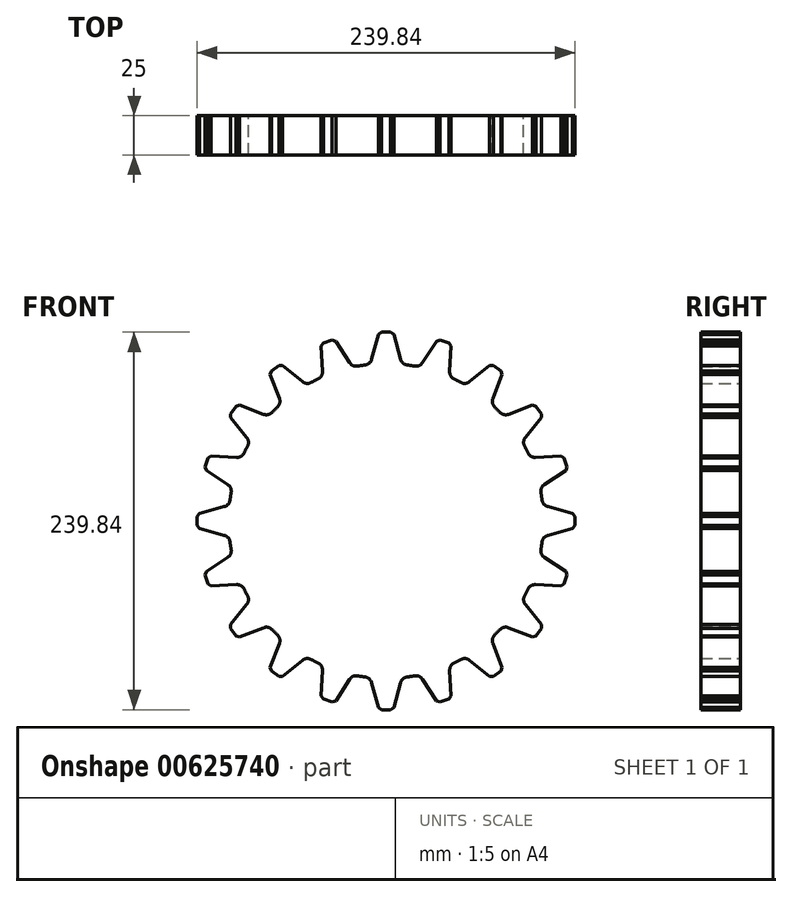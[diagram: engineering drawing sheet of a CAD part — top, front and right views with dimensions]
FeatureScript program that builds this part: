
annotation { "Feature Type Name" : "Feature", "Feature Type Description" : "" }
export const myFeature = defineFeature(function(context is Context, id is Id, definition is map)
    precondition{}
    {
        {
            var Q0;
            Q0=qCreatedBy(makeId("Front.planeOp"),FACE);
            var sketch = newSketch(context, id + "F0", { "sketchPlane" : qUnion([Q0])});
            skCircle(sketch, "E0", {"center": v(0, 0) * mm, "radius": 100 * mm});
            skCircle(sketch, "E1", {"center": v(0, 0) * mm, "radius": 120 * mm, "construction": true});
            skLineSegment(sketch, "E2", {"start": v(0, 0) * mm, "end": v(0, 167.9) * mm, "construction": true});
            skLineSegment(sketch, "E3", {"start": v(-4.5, 119.92) * mm, "end": v(-9.97, 99.5) * mm});
            skLineSegment(sketch, "E4.MirrorCS", {"start": v(4.5, 119.92) * mm, "end": v(9.97, 99.5) * mm});
            skLineSegment(sketch, "E5", {"start": v(-4.5, 119.92) * mm, "end": v(4.5, 119.92) * mm});
            skLineSegment(sketch, "E6.1.0", {"start": v(-41.34, 112.66) * mm, "end": v(-40.23, 91.55) * mm});
            skLineSegment(sketch, "E6.1.1", {"start": v(-32.78, 115.44) * mm, "end": v(-21.27, 97.71) * mm});
            skLineSegment(sketch, "E6.2.0", {"start": v(-74.13, 94.37) * mm, "end": v(-66.55, 74.64) * mm});
            skLineSegment(sketch, "E6.2.1", {"start": v(-66.84, 99.66) * mm, "end": v(-50.42, 86.36) * mm});
            skLineSegment(sketch, "E7.2.3.0", {"start": v(-99.66, 66.84) * mm, "end": v(-86.36, 50.42) * mm});
            skLineSegment(sketch, "E7.3.3.0", {"start": v(-94.37, 74.13) * mm, "end": v(-74.64, 66.55) * mm});
            skLineSegment(sketch, "E7.2.4.0", {"start": v(-115.44, 32.78) * mm, "end": v(-97.71, 21.27) * mm});
            skLineSegment(sketch, "E7.3.4.0", {"start": v(-112.66, 41.34) * mm, "end": v(-91.55, 40.23) * mm});
            skLineSegment(sketch, "E7.2.5.0", {"start": v(-119.92, -4.5) * mm, "end": v(-99.5, -9.97) * mm});
            skLineSegment(sketch, "E7.3.5.0", {"start": v(-119.92, 4.5) * mm, "end": v(-99.5, 9.97) * mm});
            skLineSegment(sketch, "E7.2.6.0", {"start": v(-112.66, -41.34) * mm, "end": v(-91.55, -40.23) * mm});
            skLineSegment(sketch, "E7.3.6.0", {"start": v(-115.44, -32.78) * mm, "end": v(-97.71, -21.27) * mm});
            skLineSegment(sketch, "E7.2.7.0", {"start": v(-94.37, -74.13) * mm, "end": v(-74.64, -66.55) * mm});
            skLineSegment(sketch, "E7.3.7.0", {"start": v(-99.66, -66.84) * mm, "end": v(-86.36, -50.42) * mm});
            skLineSegment(sketch, "E7.2.8.0", {"start": v(-66.84, -99.66) * mm, "end": v(-50.42, -86.36) * mm});
            skLineSegment(sketch, "E7.3.8.0", {"start": v(-74.13, -94.37) * mm, "end": v(-66.55, -74.64) * mm});
            skLineSegment(sketch, "E7.2.9.0", {"start": v(-32.78, -115.44) * mm, "end": v(-21.27, -97.71) * mm});
            skLineSegment(sketch, "E7.3.9.0", {"start": v(-41.34, -112.66) * mm, "end": v(-40.23, -91.55) * mm});
            skLineSegment(sketch, "E7.2.10.0", {"start": v(4.5, -119.92) * mm, "end": v(9.97, -99.5) * mm});
            skLineSegment(sketch, "E7.3.10.0", {"start": v(-4.5, -119.92) * mm, "end": v(-9.97, -99.5) * mm});
            skLineSegment(sketch, "E7.2.11.0", {"start": v(41.34, -112.66) * mm, "end": v(40.23, -91.55) * mm});
            skLineSegment(sketch, "E7.3.11.0", {"start": v(32.78, -115.44) * mm, "end": v(21.27, -97.71) * mm});
            skLineSegment(sketch, "E7.2.12.0", {"start": v(74.13, -94.37) * mm, "end": v(66.55, -74.64) * mm});
            skLineSegment(sketch, "E7.3.12.0", {"start": v(66.84, -99.66) * mm, "end": v(50.42, -86.36) * mm});
            skLineSegment(sketch, "E7.2.13.0", {"start": v(99.66, -66.84) * mm, "end": v(86.36, -50.42) * mm});
            skLineSegment(sketch, "E7.3.13.0", {"start": v(94.37, -74.13) * mm, "end": v(74.64, -66.55) * mm});
            skLineSegment(sketch, "E7.2.14.0", {"start": v(115.44, -32.78) * mm, "end": v(97.71, -21.27) * mm});
            skLineSegment(sketch, "E7.3.14.0", {"start": v(112.66, -41.34) * mm, "end": v(91.55, -40.23) * mm});
            skLineSegment(sketch, "E7.2.15.0", {"start": v(119.92, 4.5) * mm, "end": v(99.5, 9.97) * mm});
            skLineSegment(sketch, "E7.3.15.0", {"start": v(119.92, -4.5) * mm, "end": v(99.5, -9.97) * mm});
            skLineSegment(sketch, "E7.2.16.0", {"start": v(112.66, 41.34) * mm, "end": v(91.55, 40.23) * mm});
            skLineSegment(sketch, "E7.3.16.0", {"start": v(115.44, 32.78) * mm, "end": v(97.71, 21.27) * mm});
            skLineSegment(sketch, "E7.2.17.0", {"start": v(94.37, 74.13) * mm, "end": v(74.64, 66.55) * mm});
            skLineSegment(sketch, "E7.3.17.0", {"start": v(99.66, 66.84) * mm, "end": v(86.36, 50.42) * mm});
            skLineSegment(sketch, "E7.2.18.0", {"start": v(66.84, 99.66) * mm, "end": v(50.42, 86.36) * mm});
            skLineSegment(sketch, "E7.3.18.0", {"start": v(74.13, 94.37) * mm, "end": v(66.55, 74.64) * mm});
            skLineSegment(sketch, "E7.2.19.0", {"start": v(32.78, 115.44) * mm, "end": v(21.27, 97.71) * mm});
            skLineSegment(sketch, "E7.3.19.0", {"start": v(41.34, 112.66) * mm, "end": v(40.23, 91.55) * mm});
            skLineSegment(sketch, "E8", {"start": v(32.78, 115.44) * mm, "end": v(41.34, 112.66) * mm});
            skLineSegment(sketch, "E9", {"start": v(66.84, 99.66) * mm, "end": v(74.13, 94.37) * mm});
            skLineSegment(sketch, "E10", {"start": v(94.37, 74.13) * mm, "end": v(99.66, 66.84) * mm});
            skLineSegment(sketch, "E11", {"start": v(112.66, 41.34) * mm, "end": v(115.44, 32.78) * mm});
            skLineSegment(sketch, "E12", {"start": v(119.92, 4.5) * mm, "end": v(119.92, -4.5) * mm});
            skLineSegment(sketch, "E13", {"start": v(115.44, -32.78) * mm, "end": v(112.66, -41.34) * mm});
            skLineSegment(sketch, "E14", {"start": v(94.37, -74.13) * mm, "end": v(99.66, -66.84) * mm});
            skLineSegment(sketch, "E15", {"start": v(74.13, -94.37) * mm, "end": v(66.84, -99.66) * mm});
            skLineSegment(sketch, "E16", {"start": v(41.34, -112.66) * mm, "end": v(32.78, -115.44) * mm});
            skLineSegment(sketch, "E17", {"start": v(4.5, -119.92) * mm, "end": v(-4.5, -119.92) * mm});
            skLineSegment(sketch, "E18", {"start": v(-32.78, -115.44) * mm, "end": v(-41.34, -112.66) * mm});
            skLineSegment(sketch, "E19", {"start": v(-66.84, -99.66) * mm, "end": v(-74.13, -94.37) * mm});
            skLineSegment(sketch, "E20", {"start": v(-94.37, -74.13) * mm, "end": v(-99.66, -66.84) * mm});
            skLineSegment(sketch, "E21", {"start": v(-112.66, -41.34) * mm, "end": v(-115.44, -32.78) * mm});
            skLineSegment(sketch, "E22", {"start": v(-119.92, -4.5) * mm, "end": v(-119.92, 4.5) * mm});
            skLineSegment(sketch, "E23", {"start": v(-115.44, 32.78) * mm, "end": v(-112.66, 41.34) * mm});
            skLineSegment(sketch, "E24", {"start": v(-99.66, 66.84) * mm, "end": v(-94.37, 74.13) * mm});
            skLineSegment(sketch, "E25", {"start": v(-74.13, 94.37) * mm, "end": v(-66.84, 99.66) * mm});
            skLineSegment(sketch, "E26", {"start": v(-41.34, 112.66) * mm, "end": v(-32.78, 115.44) * mm});
            skSolve(sketch);
        }
        {
            var Q0;
            Q0 = qSketchRegion(id + "F0", true);
            extrude(context, id + "F1", {"entities" : qUnion([Q0]), "depth" : 25 * mm, "offsetDistance" : 25 * mm});
        }
        {
            var Q0;
            Q0=makeQuery(id+"F1.opExtrude","SWEPT_EDGE",EDGE,{"disambiguationData":[OSD([sQuery(id+"F0.wireOp",EDGE,"E7.2.18.0"),sQuery(id+"F0.wireOp",EDGE,"E9")])]});
            var Q1;
            Q1=makeQuery(id+"F1.opExtrude","SWEPT_EDGE",EDGE,{"disambiguationData":[OSD([sQuery(id+"F0.wireOp",EDGE,"E7.3.18.0"),sQuery(id+"F0.wireOp",EDGE,"E9")])]});
            chamfer(context, id + "F2", {"entities" : qUnion([Q0, Q1]), "width" : 2 * mm, "tangentPropagation" : true});
        }
        {
            var Q0;
            Q0=makeQuery(id+"F1.opExtrude","SWEPT_EDGE",EDGE,{"disambiguationData":[OSD([sQuery(id+"F0.wireOp",EDGE,"E7.2.17.0"),sQuery(id+"F0.wireOp",EDGE,"E10")])]});
            var Q1;
            Q1=makeQuery(id+"F1.opExtrude","SWEPT_EDGE",EDGE,{"disambiguationData":[OSD([sQuery(id+"F0.wireOp",EDGE,"E7.3.17.0"),sQuery(id+"F0.wireOp",EDGE,"E10")])]});
            var Q2;
            Q2=makeQuery(id+"F1.opExtrude","SWEPT_EDGE",EDGE,{"disambiguationData":[OSD([sQuery(id+"F0.wireOp",EDGE,"E7.2.16.0"),sQuery(id+"F0.wireOp",EDGE,"E11")])]});
            var Q3;
            Q3=makeQuery(id+"F1.opExtrude","SWEPT_EDGE",EDGE,{"disambiguationData":[OSD([sQuery(id+"F0.wireOp",EDGE,"E7.3.16.0"),sQuery(id+"F0.wireOp",EDGE,"E11")])]});
            var Q4;
            Q4=makeQuery(id+"F1.opExtrude","SWEPT_EDGE",EDGE,{"disambiguationData":[OSD([sQuery(id+"F0.wireOp",EDGE,"E7.2.15.0"),sQuery(id+"F0.wireOp",EDGE,"E12")])]});
            var Q5;
            Q5=makeQuery(id+"F1.opExtrude","SWEPT_EDGE",EDGE,{"disambiguationData":[OSD([sQuery(id+"F0.wireOp",EDGE,"E7.3.15.0"),sQuery(id+"F0.wireOp",EDGE,"E12")])]});
            var Q6;
            Q6=makeQuery(id+"F1.opExtrude","SWEPT_EDGE",EDGE,{"disambiguationData":[OSD([sQuery(id+"F0.wireOp",EDGE,"E7.2.14.0"),sQuery(id+"F0.wireOp",EDGE,"E13")])]});
            var Q7;
            Q7=makeQuery(id+"F1.opExtrude","SWEPT_EDGE",EDGE,{"disambiguationData":[OSD([sQuery(id+"F0.wireOp",EDGE,"E7.3.14.0"),sQuery(id+"F0.wireOp",EDGE,"E13")])]});
            var Q8;
            Q8=makeQuery(id+"F1.opExtrude","SWEPT_EDGE",EDGE,{"disambiguationData":[OSD([sQuery(id+"F0.wireOp",EDGE,"E7.2.13.0"),sQuery(id+"F0.wireOp",EDGE,"E14")])]});
            var Q9;
            Q9=makeQuery(id+"F1.opExtrude","SWEPT_EDGE",EDGE,{"disambiguationData":[OSD([sQuery(id+"F0.wireOp",EDGE,"E7.3.13.0"),sQuery(id+"F0.wireOp",EDGE,"E14")])]});
            var Q10;
            Q10=makeQuery(id+"F1.opExtrude","SWEPT_EDGE",EDGE,{"disambiguationData":[OSD([sQuery(id+"F0.wireOp",EDGE,"E7.2.12.0"),sQuery(id+"F0.wireOp",EDGE,"E15")])]});
            var Q11;
            Q11=makeQuery(id+"F1.opExtrude","SWEPT_EDGE",EDGE,{"disambiguationData":[OSD([sQuery(id+"F0.wireOp",EDGE,"E7.3.12.0"),sQuery(id+"F0.wireOp",EDGE,"E15")])]});
            var Q12;
            Q12=makeQuery(id+"F1.opExtrude","SWEPT_EDGE",EDGE,{"disambiguationData":[OSD([sQuery(id+"F0.wireOp",EDGE,"E7.2.11.0"),sQuery(id+"F0.wireOp",EDGE,"E16")])]});
            var Q13;
            Q13=makeQuery(id+"F1.opExtrude","SWEPT_EDGE",EDGE,{"disambiguationData":[OSD([sQuery(id+"F0.wireOp",EDGE,"E7.3.11.0"),sQuery(id+"F0.wireOp",EDGE,"E16")])]});
            chamfer(context, id + "F3", {"entities" : qUnion([Q0, Q1, Q2, Q3, Q4, Q5, Q6, Q7, Q8, Q9, Q10, Q11, Q12, Q13]), "width" : 2 * mm, "tangentPropagation" : true});
        }
        {
            var Q0;
            Q0=makeQuery(id+"F1.opExtrude","SWEPT_EDGE",EDGE,{"disambiguationData":[OSD([sQuery(id+"F0.wireOp",EDGE,"E7.2.10.0"),sQuery(id+"F0.wireOp",EDGE,"E17")])]});
            var Q1;
            Q1=makeQuery(id+"F1.opExtrude","SWEPT_EDGE",EDGE,{"disambiguationData":[OSD([sQuery(id+"F0.wireOp",EDGE,"E7.3.10.0"),sQuery(id+"F0.wireOp",EDGE,"E17")])]});
            var Q2;
            Q2=makeQuery(id+"F1.opExtrude","SWEPT_EDGE",EDGE,{"disambiguationData":[OSD([sQuery(id+"F0.wireOp",EDGE,"E7.2.9.0"),sQuery(id+"F0.wireOp",EDGE,"E18")])]});
            var Q3;
            Q3=makeQuery(id+"F1.opExtrude","SWEPT_EDGE",EDGE,{"disambiguationData":[OSD([sQuery(id+"F0.wireOp",EDGE,"E7.3.9.0"),sQuery(id+"F0.wireOp",EDGE,"E18")])]});
            var Q4;
            Q4=makeQuery(id+"F1.opExtrude","SWEPT_EDGE",EDGE,{"disambiguationData":[OSD([sQuery(id+"F0.wireOp",EDGE,"E7.2.8.0"),sQuery(id+"F0.wireOp",EDGE,"E19")])]});
            var Q5;
            Q5=makeQuery(id+"F1.opExtrude","SWEPT_EDGE",EDGE,{"disambiguationData":[OSD([sQuery(id+"F0.wireOp",EDGE,"E7.3.8.0"),sQuery(id+"F0.wireOp",EDGE,"E19")])]});
            var Q6;
            Q6=makeQuery(id+"F1.opExtrude","SWEPT_EDGE",EDGE,{"disambiguationData":[OSD([sQuery(id+"F0.wireOp",EDGE,"E7.2.7.0"),sQuery(id+"F0.wireOp",EDGE,"E20")])]});
            var Q7;
            Q7=makeQuery(id+"F1.opExtrude","SWEPT_EDGE",EDGE,{"disambiguationData":[OSD([sQuery(id+"F0.wireOp",EDGE,"E7.3.7.0"),sQuery(id+"F0.wireOp",EDGE,"E20")])]});
            var Q8;
            Q8=makeQuery(id+"F1.opExtrude","SWEPT_EDGE",EDGE,{"disambiguationData":[OSD([sQuery(id+"F0.wireOp",EDGE,"E7.2.6.0"),sQuery(id+"F0.wireOp",EDGE,"E21")])]});
            var Q9;
            Q9=makeQuery(id+"F1.opExtrude","SWEPT_EDGE",EDGE,{"disambiguationData":[OSD([sQuery(id+"F0.wireOp",EDGE,"E7.3.6.0"),sQuery(id+"F0.wireOp",EDGE,"E21")])]});
            var Q10;
            Q10=makeQuery(id+"F1.opExtrude","SWEPT_EDGE",EDGE,{"disambiguationData":[OSD([sQuery(id+"F0.wireOp",EDGE,"E7.2.5.0"),sQuery(id+"F0.wireOp",EDGE,"E22")])]});
            var Q11;
            Q11=makeQuery(id+"F1.opExtrude","SWEPT_EDGE",EDGE,{"disambiguationData":[OSD([sQuery(id+"F0.wireOp",EDGE,"E7.3.5.0"),sQuery(id+"F0.wireOp",EDGE,"E22")])]});
            var Q12;
            Q12=makeQuery(id+"F1.opExtrude","SWEPT_EDGE",EDGE,{"disambiguationData":[OSD([sQuery(id+"F0.wireOp",EDGE,"E7.2.4.0"),sQuery(id+"F0.wireOp",EDGE,"E23")])]});
            var Q13;
            Q13=makeQuery(id+"F1.opExtrude","SWEPT_EDGE",EDGE,{"disambiguationData":[OSD([sQuery(id+"F0.wireOp",EDGE,"E7.3.4.0"),sQuery(id+"F0.wireOp",EDGE,"E23")])]});
            var Q14;
            Q14=makeQuery(id+"F1.opExtrude","SWEPT_EDGE",EDGE,{"disambiguationData":[OSD([sQuery(id+"F0.wireOp",EDGE,"E7.2.3.0"),sQuery(id+"F0.wireOp",EDGE,"E24")])]});
            var Q15;
            Q15=makeQuery(id+"F1.opExtrude","SWEPT_EDGE",EDGE,{"disambiguationData":[OSD([sQuery(id+"F0.wireOp",EDGE,"E7.3.3.0"),sQuery(id+"F0.wireOp",EDGE,"E24")])]});
            var Q16;
            Q16=makeQuery(id+"F1.opExtrude","SWEPT_EDGE",EDGE,{"disambiguationData":[OSD([sQuery(id+"F0.wireOp",EDGE,"E6.2.0"),sQuery(id+"F0.wireOp",EDGE,"E25")])]});
            var Q17;
            Q17=makeQuery(id+"F1.opExtrude","SWEPT_EDGE",EDGE,{"disambiguationData":[OSD([sQuery(id+"F0.wireOp",EDGE,"E6.2.1"),sQuery(id+"F0.wireOp",EDGE,"E25")])]});
            chamfer(context, id + "F4", {"entities" : qUnion([Q0, Q1, Q2, Q3, Q4, Q5, Q6, Q7, Q8, Q9, Q10, Q11, Q12, Q13, Q14, Q15, Q16, Q17]), "width" : 2 * mm, "tangentPropagation" : true});
        }
        {
            var Q0;
            Q0=makeQuery(id+"F1.opExtrude","SWEPT_EDGE",EDGE,{"disambiguationData":[OSD([sQuery(id+"F0.wireOp",EDGE,"E6.1.0"),sQuery(id+"F0.wireOp",EDGE,"E26")])]});
            var Q1;
            Q1=makeQuery(id+"F1.opExtrude","SWEPT_EDGE",EDGE,{"disambiguationData":[OSD([sQuery(id+"F0.wireOp",EDGE,"E6.1.1"),sQuery(id+"F0.wireOp",EDGE,"E26")])]});
            var Q2;
            Q2=makeQuery(id+"F1.opExtrude","SWEPT_EDGE",EDGE,{"disambiguationData":[OSD([sQuery(id+"F0.wireOp",EDGE,"E3"),sQuery(id+"F0.wireOp",EDGE,"E5")])]});
            var Q3;
            Q3=makeQuery(id+"F1.opExtrude","SWEPT_EDGE",EDGE,{"disambiguationData":[OSD([sQuery(id+"F0.wireOp",EDGE,"E4.MirrorCS"),sQuery(id+"F0.wireOp",EDGE,"E5")])]});
            var Q4;
            Q4=makeQuery(id+"F1.opExtrude","SWEPT_EDGE",EDGE,{"disambiguationData":[OSD([sQuery(id+"F0.wireOp",EDGE,"E7.2.19.0"),sQuery(id+"F0.wireOp",EDGE,"E8")])]});
            var Q5;
            Q5=makeQuery(id+"F1.opExtrude","SWEPT_EDGE",EDGE,{"disambiguationData":[OSD([sQuery(id+"F0.wireOp",EDGE,"E7.3.19.0"),sQuery(id+"F0.wireOp",EDGE,"E8")])]});
            chamfer(context, id + "F5", {"entities" : qUnion([Q0, Q1, Q2, Q3, Q4, Q5]), "width" : 2 * mm, "tangentPropagation" : true});
        }
        {
            var Q0;
            Q0=makeQuery(id+"F1.opExtrude","SWEPT_EDGE",EDGE,{"disambiguationData":[OSD([sQuery(id+"F0.wireOp",EDGE,"E0"),sQuery(id+"F0.wireOp",EDGE,"E6.2.1")])]});
            var Q1;
            Q1=makeQuery(id+"F1.opExtrude","SWEPT_EDGE",EDGE,{"disambiguationData":[OSD([sQuery(id+"F0.wireOp",EDGE,"E0"),sQuery(id+"F0.wireOp",EDGE,"E6.1.0")])]});
            var Q2;
            Q2=makeQuery(id+"F1.opExtrude","SWEPT_EDGE",EDGE,{"disambiguationData":[OSD([sQuery(id+"F0.wireOp",EDGE,"E0"),sQuery(id+"F0.wireOp",EDGE,"E6.1.1")])]});
            var Q3;
            Q3=makeQuery(id+"F1.opExtrude","SWEPT_EDGE",EDGE,{"disambiguationData":[OSD([sQuery(id+"F0.wireOp",EDGE,"E0"),sQuery(id+"F0.wireOp",EDGE,"E3")])]});
            var Q4;
            Q4=makeQuery(id+"F1.opExtrude","SWEPT_EDGE",EDGE,{"disambiguationData":[OSD([sQuery(id+"F0.wireOp",EDGE,"E0"),sQuery(id+"F0.wireOp",EDGE,"E4.MirrorCS")])]});
            var Q5;
            Q5=makeQuery(id+"F1.opExtrude","SWEPT_EDGE",EDGE,{"disambiguationData":[OSD([sQuery(id+"F0.wireOp",EDGE,"E0"),sQuery(id+"F0.wireOp",EDGE,"E7.2.19.0")])]});
            var Q6;
            Q6=makeQuery(id+"F1.opExtrude","SWEPT_EDGE",EDGE,{"disambiguationData":[OSD([sQuery(id+"F0.wireOp",EDGE,"E0"),sQuery(id+"F0.wireOp",EDGE,"E7.3.19.0")])]});
            var Q7;
            Q7=makeQuery(id+"F1.opExtrude","SWEPT_EDGE",EDGE,{"disambiguationData":[OSD([sQuery(id+"F0.wireOp",EDGE,"E0"),sQuery(id+"F0.wireOp",EDGE,"E7.2.18.0")])]});
            var Q8;
            Q8=makeQuery(id+"F1.opExtrude","SWEPT_EDGE",EDGE,{"disambiguationData":[OSD([sQuery(id+"F0.wireOp",EDGE,"E0"),sQuery(id+"F0.wireOp",EDGE,"E7.3.18.0")])]});
            var Q9;
            Q9=makeQuery(id+"F1.opExtrude","SWEPT_EDGE",EDGE,{"disambiguationData":[OSD([sQuery(id+"F0.wireOp",EDGE,"E0"),sQuery(id+"F0.wireOp",EDGE,"E7.2.17.0")])]});
            var Q10;
            Q10=makeQuery(id+"F1.opExtrude","SWEPT_EDGE",EDGE,{"disambiguationData":[OSD([sQuery(id+"F0.wireOp",EDGE,"E0"),sQuery(id+"F0.wireOp",EDGE,"E7.3.17.0")])]});
            var Q11;
            Q11=makeQuery(id+"F1.opExtrude","SWEPT_EDGE",EDGE,{"disambiguationData":[OSD([sQuery(id+"F0.wireOp",EDGE,"E0"),sQuery(id+"F0.wireOp",EDGE,"E7.2.16.0")])]});
            var Q12;
            Q12=makeQuery(id+"F1.opExtrude","SWEPT_EDGE",EDGE,{"disambiguationData":[OSD([sQuery(id+"F0.wireOp",EDGE,"E0"),sQuery(id+"F0.wireOp",EDGE,"E7.3.16.0")])]});
            var Q13;
            Q13=makeQuery(id+"F1.opExtrude","SWEPT_EDGE",EDGE,{"disambiguationData":[OSD([sQuery(id+"F0.wireOp",EDGE,"E0"),sQuery(id+"F0.wireOp",EDGE,"E7.2.15.0")])]});
            var Q14;
            Q14=makeQuery(id+"F1.opExtrude","SWEPT_EDGE",EDGE,{"disambiguationData":[OSD([sQuery(id+"F0.wireOp",EDGE,"E0"),sQuery(id+"F0.wireOp",EDGE,"E7.3.15.0")])]});
            var Q15;
            Q15=makeQuery(id+"F1.opExtrude","SWEPT_EDGE",EDGE,{"disambiguationData":[OSD([sQuery(id+"F0.wireOp",EDGE,"E0"),sQuery(id+"F0.wireOp",EDGE,"E7.2.14.0")])]});
            var Q16;
            Q16=makeQuery(id+"F1.opExtrude","SWEPT_EDGE",EDGE,{"disambiguationData":[OSD([sQuery(id+"F0.wireOp",EDGE,"E0"),sQuery(id+"F0.wireOp",EDGE,"E7.3.14.0")])]});
            var Q17;
            Q17=makeQuery(id+"F1.opExtrude","SWEPT_EDGE",EDGE,{"disambiguationData":[OSD([sQuery(id+"F0.wireOp",EDGE,"E0"),sQuery(id+"F0.wireOp",EDGE,"E7.2.13.0")])]});
            var Q18;
            Q18=makeQuery(id+"F1.opExtrude","SWEPT_EDGE",EDGE,{"disambiguationData":[OSD([sQuery(id+"F0.wireOp",EDGE,"E0"),sQuery(id+"F0.wireOp",EDGE,"E7.3.13.0")])]});
            var Q19;
            Q19=makeQuery(id+"F1.opExtrude","SWEPT_EDGE",EDGE,{"disambiguationData":[OSD([sQuery(id+"F0.wireOp",EDGE,"E0"),sQuery(id+"F0.wireOp",EDGE,"E7.2.12.0")])]});
            var Q20;
            Q20=makeQuery(id+"F1.opExtrude","SWEPT_EDGE",EDGE,{"disambiguationData":[OSD([sQuery(id+"F0.wireOp",EDGE,"E0"),sQuery(id+"F0.wireOp",EDGE,"E7.3.12.0")])]});
            var Q21;
            Q21=makeQuery(id+"F1.opExtrude","SWEPT_EDGE",EDGE,{"disambiguationData":[OSD([sQuery(id+"F0.wireOp",EDGE,"E0"),sQuery(id+"F0.wireOp",EDGE,"E7.2.11.0")])]});
            var Q22;
            Q22=makeQuery(id+"F1.opExtrude","SWEPT_EDGE",EDGE,{"disambiguationData":[OSD([sQuery(id+"F0.wireOp",EDGE,"E0"),sQuery(id+"F0.wireOp",EDGE,"E7.3.11.0")])]});
            var Q23;
            Q23=makeQuery(id+"F1.opExtrude","SWEPT_EDGE",EDGE,{"disambiguationData":[OSD([sQuery(id+"F0.wireOp",EDGE,"E0"),sQuery(id+"F0.wireOp",EDGE,"E7.2.10.0")])]});
            var Q24;
            Q24=makeQuery(id+"F1.opExtrude","SWEPT_EDGE",EDGE,{"disambiguationData":[OSD([sQuery(id+"F0.wireOp",EDGE,"E0"),sQuery(id+"F0.wireOp",EDGE,"E7.3.10.0")])]});
            var Q25;
            Q25=makeQuery(id+"F1.opExtrude","SWEPT_EDGE",EDGE,{"disambiguationData":[OSD([sQuery(id+"F0.wireOp",EDGE,"E0"),sQuery(id+"F0.wireOp",EDGE,"E7.2.9.0")])]});
            var Q26;
            Q26=makeQuery(id+"F1.opExtrude","SWEPT_EDGE",EDGE,{"disambiguationData":[OSD([sQuery(id+"F0.wireOp",EDGE,"E0"),sQuery(id+"F0.wireOp",EDGE,"E7.3.9.0")])]});
            var Q27;
            Q27=makeQuery(id+"F1.opExtrude","SWEPT_EDGE",EDGE,{"disambiguationData":[OSD([sQuery(id+"F0.wireOp",EDGE,"E0"),sQuery(id+"F0.wireOp",EDGE,"E7.2.8.0")])]});
            var Q28;
            Q28=makeQuery(id+"F1.opExtrude","SWEPT_EDGE",EDGE,{"disambiguationData":[OSD([sQuery(id+"F0.wireOp",EDGE,"E0"),sQuery(id+"F0.wireOp",EDGE,"E7.3.8.0")])]});
            var Q29;
            Q29=makeQuery(id+"F1.opExtrude","SWEPT_EDGE",EDGE,{"disambiguationData":[OSD([sQuery(id+"F0.wireOp",EDGE,"E0"),sQuery(id+"F0.wireOp",EDGE,"E7.2.7.0")])]});
            var Q30;
            Q30=makeQuery(id+"F1.opExtrude","SWEPT_EDGE",EDGE,{"disambiguationData":[OSD([sQuery(id+"F0.wireOp",EDGE,"E0"),sQuery(id+"F0.wireOp",EDGE,"E7.3.7.0")])]});
            var Q31;
            Q31=makeQuery(id+"F1.opExtrude","SWEPT_EDGE",EDGE,{"disambiguationData":[OSD([sQuery(id+"F0.wireOp",EDGE,"E0"),sQuery(id+"F0.wireOp",EDGE,"E7.2.6.0")])]});
            var Q32;
            Q32=makeQuery(id+"F1.opExtrude","SWEPT_EDGE",EDGE,{"disambiguationData":[OSD([sQuery(id+"F0.wireOp",EDGE,"E0"),sQuery(id+"F0.wireOp",EDGE,"E7.3.6.0")])]});
            var Q33;
            Q33=makeQuery(id+"F1.opExtrude","SWEPT_EDGE",EDGE,{"disambiguationData":[OSD([sQuery(id+"F0.wireOp",EDGE,"E0"),sQuery(id+"F0.wireOp",EDGE,"E7.2.5.0")])]});
            var Q34;
            Q34=makeQuery(id+"F1.opExtrude","SWEPT_EDGE",EDGE,{"disambiguationData":[OSD([sQuery(id+"F0.wireOp",EDGE,"E0"),sQuery(id+"F0.wireOp",EDGE,"E7.3.5.0")])]});
            var Q35;
            Q35=makeQuery(id+"F1.opExtrude","SWEPT_EDGE",EDGE,{"disambiguationData":[OSD([sQuery(id+"F0.wireOp",EDGE,"E0"),sQuery(id+"F0.wireOp",EDGE,"E7.2.4.0")])]});
            var Q36;
            Q36=makeQuery(id+"F1.opExtrude","SWEPT_EDGE",EDGE,{"disambiguationData":[OSD([sQuery(id+"F0.wireOp",EDGE,"E0"),sQuery(id+"F0.wireOp",EDGE,"E7.3.4.0")])]});
            var Q37;
            Q37=makeQuery(id+"F1.opExtrude","SWEPT_EDGE",EDGE,{"disambiguationData":[OSD([sQuery(id+"F0.wireOp",EDGE,"E0"),sQuery(id+"F0.wireOp",EDGE,"E7.2.3.0")])]});
            var Q38;
            Q38=makeQuery(id+"F1.opExtrude","SWEPT_EDGE",EDGE,{"disambiguationData":[OSD([sQuery(id+"F0.wireOp",EDGE,"E0"),sQuery(id+"F0.wireOp",EDGE,"E7.3.3.0")])]});
            var Q39;
            Q39=makeQuery(id+"F1.opExtrude","SWEPT_EDGE",EDGE,{"disambiguationData":[OSD([sQuery(id+"F0.wireOp",EDGE,"E0"),sQuery(id+"F0.wireOp",EDGE,"E6.2.0")])]});
            fillet(context, id + "F6", {"entities" : qUnion([Q0, Q1, Q2, Q3, Q4, Q5, Q6, Q7, Q8, Q9, Q10, Q11, Q12, Q13, Q14, Q15, Q16, Q17, Q18, Q19, Q20, Q21, Q22, Q23, Q24, Q25, Q26, Q27, Q28, Q29, Q30, Q31, Q32, Q33, Q34, Q35, Q36, Q37, Q38, Q39]), "radius" : 5 * mm, "tangentPropagation" : true, "allowEdgeOverflow" : false});
        }
    });
